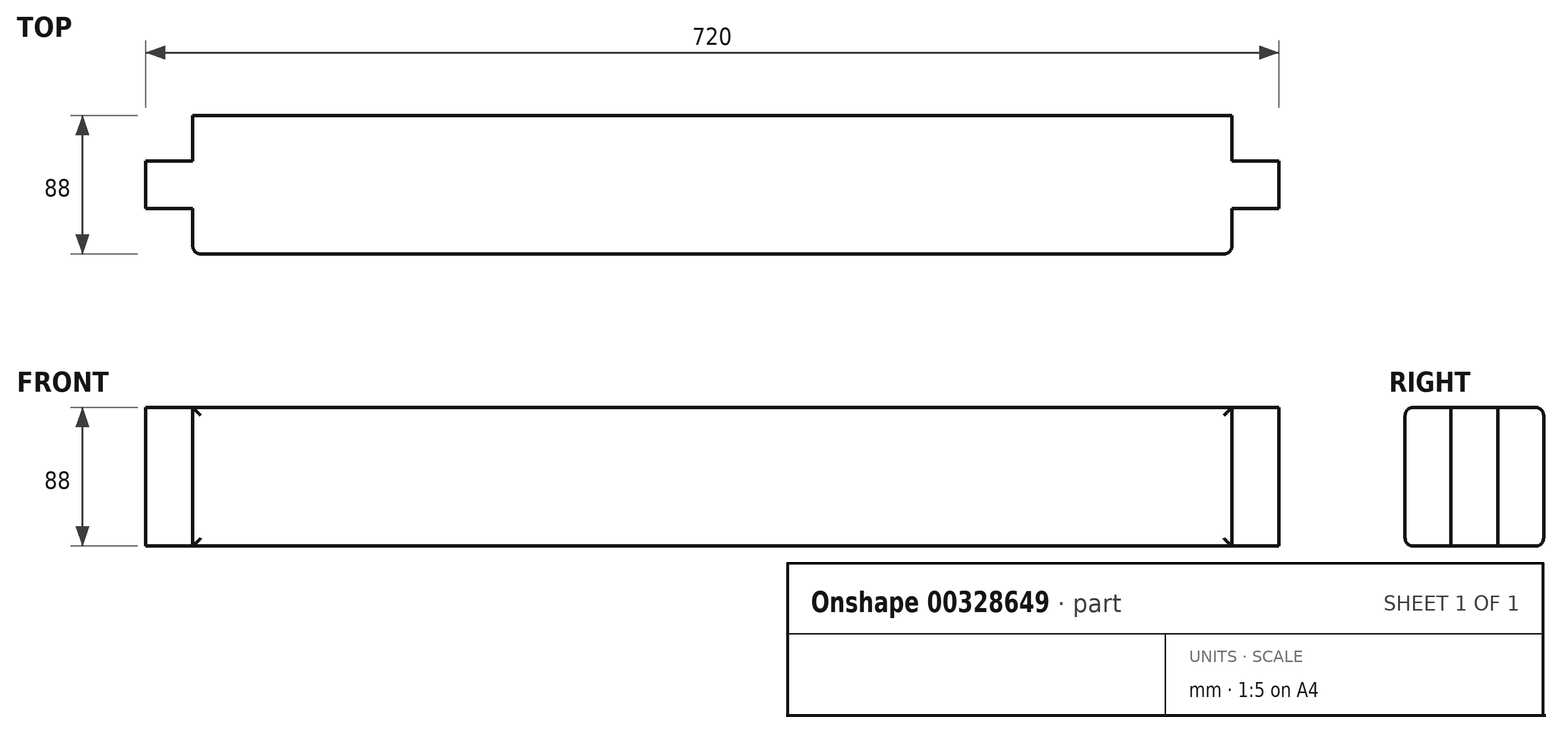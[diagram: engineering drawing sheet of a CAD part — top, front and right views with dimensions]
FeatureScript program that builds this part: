
annotation { "Feature Type Name" : "Feature", "Feature Type Description" : "" }
export const myFeature = defineFeature(function(context is Context, id is Id, definition is map)
    precondition{}
    {
        {
            var Q0;
            Q0=qCreatedBy(makeId("Right.planeOp"),FACE);
            var sketch = newSketch(context, id + "F0", { "sketchPlane" : qUnion([Q0])});
            skLineSegment(sketch, "E0.bottom", {"start": v(0, 0) * mm, "end": v(88, 0) * mm});
            skLineSegment(sketch, "E0.top", {"start": v(0, 88) * mm, "end": v(88, 88) * mm});
            skLineSegment(sketch, "E0.left", {"start": v(0, 0) * mm, "end": v(0, 88) * mm});
            skLineSegment(sketch, "E0.right", {"start": v(88, 0) * mm, "end": v(88, 88) * mm});
            skSolve(sketch);
        }
        {
            var Q0;
            Q0=qSketchRegion(id+"F0",true);
            extrude(context, id + "F1", {"entities" : qUnion([Q0]), "depth" : 720 * mm});
        }
        {
            var Q0;
            Q0=makeQuery(id+"F1.opExtrude","SWEPT_FACE",FACE,{"disambiguationData":[OSD([sQuery(id+"F0.wireOp",EDGE,"E0.top")])]});
            var sketch = newSketch(context, id + "F2", { "sketchPlane" : qUnion([Q0])});
            skLineSegment(sketch, "E1.bottom", {"start": v(720, 0) * mm, "end": v(690, 0) * mm});
            skLineSegment(sketch, "E1.top", {"start": v(720, 29) * mm, "end": v(690, 29) * mm});
            skLineSegment(sketch, "E1.left", {"start": v(720, 0) * mm, "end": v(720, 29) * mm});
            skLineSegment(sketch, "E1.right", {"start": v(690, 0) * mm, "end": v(690, 29) * mm});
            skLineSegment(sketch, "E2.bottom", {"start": v(720, 88) * mm, "end": v(690, 88) * mm});
            skLineSegment(sketch, "E2.top", {"start": v(720, 59) * mm, "end": v(690, 59) * mm});
            skLineSegment(sketch, "E2.left", {"start": v(720, 88) * mm, "end": v(720, 59) * mm});
            skLineSegment(sketch, "E2.right", {"start": v(690, 88) * mm, "end": v(690, 59) * mm});
            skSolve(sketch);
        }
        {
            var Q0;
            Q0=qSketchRegion(id+"F2",true);
            extrude(context, id + "F3", {"entities" : qUnion([Q0]), "operationType" : NewBodyOperationType.REMOVE, "endBound" : BoundingType.THROUGH_ALL, "oppositeDirection" : true, "depth" : 25 * mm});
        }
        {
            var Q0;
            Q0=makeQuery(id+"F1.opExtrude","SWEPT_FACE",FACE,{"disambiguationData":[OSD([sQuery(id+"F0.wireOp",EDGE,"E0.top")])]});
            var sketch = newSketch(context, id + "F4", { "sketchPlane" : qUnion([Q0])});
            skLineSegment(sketch, "E3.bottom", {"start": v(0, 88) * mm, "end": v(30, 88) * mm});
            skLineSegment(sketch, "E3.top", {"start": v(0, 59) * mm, "end": v(30, 59) * mm});
            skLineSegment(sketch, "E3.left", {"start": v(0, 88) * mm, "end": v(0, 59) * mm});
            skLineSegment(sketch, "E3.right", {"start": v(30, 88) * mm, "end": v(30, 59) * mm});
            skLineSegment(sketch, "E4.bottom", {"start": v(0, 0) * mm, "end": v(30, 0) * mm});
            skLineSegment(sketch, "E4.top", {"start": v(0, 29) * mm, "end": v(30, 29) * mm});
            skLineSegment(sketch, "E4.left", {"start": v(0, 0) * mm, "end": v(0, 29) * mm});
            skLineSegment(sketch, "E4.right", {"start": v(30, 0) * mm, "end": v(30, 29) * mm});
            skSolve(sketch);
        }
        {
            var Q0;
            Q0=makeQuery(id+"F4.imprint","IMPRINT",FACE,{"disambiguationData":[TD([[makeQuery(id+"F4.imprint","IMPRINT",EDGE,{"derivedFrom":sQuery(id+"F4.wireOp",EDGE,"E3.bottom")}),1.0]])]});
            var Q1;
            Q1=makeQuery(id+"F4.imprint","IMPRINT",FACE,{"disambiguationData":[TD([[makeQuery(id+"F4.imprint","IMPRINT",EDGE,{"derivedFrom":sQuery(id+"F4.wireOp",EDGE,"E4.bottom")}),-1.0]])]});
            extrude(context, id + "F5", {"entities" : qUnion([Q0, Q1]), "operationType" : NewBodyOperationType.REMOVE, "endBound" : BoundingType.THROUGH_ALL, "oppositeDirection" : true, "depth" : 80.17 * mm});
        }
        {
            var Q0;
            Q0=makeQuery(id+"F1.opExtrude","SWEPT_FACE",FACE,{"disambiguationData":[OSD([sQuery(id+"F0.wireOp",EDGE,"E0.left")])]});
            var Q1;
            Q1=makeQuery(id+"F1.opExtrude","SWEPT_EDGE",EDGE,{"disambiguationData":[OSD([sQuery(id+"F0.wireOp",EDGE,"E0.bottom"),sQuery(id+"F0.wireOp",EDGE,"E0.left")])]});
            var Q2;
            Q2=makeQuery(id+"F1.opExtrude","SWEPT_EDGE",EDGE,{"disambiguationData":[OSD([sQuery(id+"F0.wireOp",EDGE,"E0.top"),sQuery(id+"F0.wireOp",EDGE,"E0.left")])]});
            var Q3;
            Q3=makeQuery(id+"F1.opExtrude","SWEPT_EDGE",EDGE,{"disambiguationData":[OSD([sQuery(id+"F0.wireOp",EDGE,"E0.top"),sQuery(id+"F0.wireOp",EDGE,"E0.right")])]});
            var Q4;
            Q4=makeQuery(id+"F1.opExtrude","SWEPT_EDGE",EDGE,{"disambiguationData":[OSD([sQuery(id+"F0.wireOp",EDGE,"E0.bottom"),sQuery(id+"F0.wireOp",EDGE,"E0.right")])]});
            var Q5;
            Q5=makeQuery(id+"F3.boolean.opBoolean","COPY",EDGE,{"derivedFrom":makeQuery(id+"F3.opExtrude","SWEPT_EDGE",EDGE,{"disambiguationData":[OSD([sQuery(id+"F0.wireOp",EDGE,"E0.top"),sQuery(id+"F0.wireOp",EDGE,"E0.right"),sQuery(id+"F2.wireOp",EDGE,"E2.bottom"),sQuery(id+"F2.wireOp",EDGE,"E2.right")])]})});
            var Q6;
            Q6=makeQuery(id+"F5.boolean.opBoolean","COPY",EDGE,{"derivedFrom":makeQuery(id+"F5.opExtrude","SWEPT_EDGE",EDGE,{"disambiguationData":[OSD([sQuery(id+"F0.wireOp",EDGE,"E0.top"),sQuery(id+"F0.wireOp",EDGE,"E0.right"),sQuery(id+"F4.wireOp",EDGE,"E3.bottom"),sQuery(id+"F4.wireOp",EDGE,"E3.right")])]})});
            var Q7;
            Q7=makeQuery(id+"F5.boolean.opBoolean","COPY",EDGE,{"derivedFrom":makeQuery(id+"F5.opExtrude","SWEPT_EDGE",EDGE,{"disambiguationData":[OSD([sQuery(id+"F0.wireOp",EDGE,"E0.top"),sQuery(id+"F0.wireOp",EDGE,"E0.left"),sQuery(id+"F4.wireOp",EDGE,"E4.bottom"),sQuery(id+"F4.wireOp",EDGE,"E4.right")])]})});
            var Q8;
            Q8=makeQuery(id+"F3.boolean.opBoolean","COPY",EDGE,{"derivedFrom":makeQuery(id+"F3.opExtrude","SWEPT_EDGE",EDGE,{"disambiguationData":[OSD([sQuery(id+"F0.wireOp",EDGE,"E0.top"),sQuery(id+"F0.wireOp",EDGE,"E0.left"),sQuery(id+"F2.wireOp",EDGE,"E1.bottom"),sQuery(id+"F2.wireOp",EDGE,"E1.right")])]})});
            fillet(context, id + "F6", {"entities" : qUnion([Q0, Q1, Q2, Q3, Q4, Q5, Q6, Q7, Q8]), "radius" : 5 * mm, "tangentPropagation" : true, "allowEdgeOverflow" : false});
        }
    });
